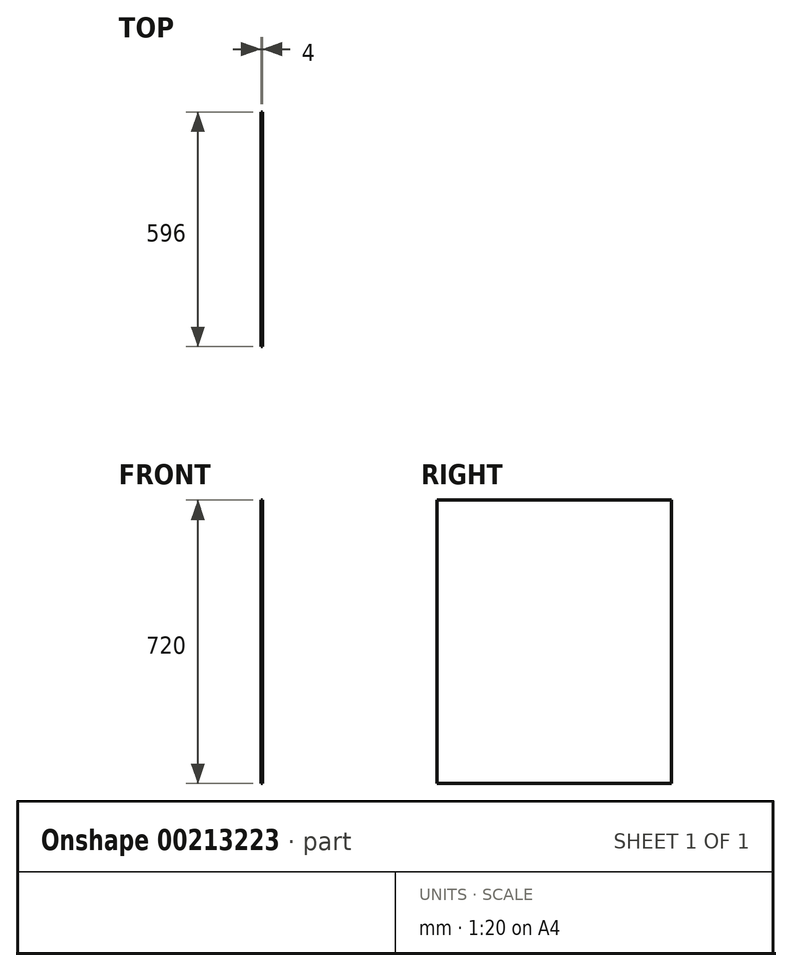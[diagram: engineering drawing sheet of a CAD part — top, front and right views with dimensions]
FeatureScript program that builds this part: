
annotation { "Feature Type Name" : "Feature", "Feature Type Description" : "" }
export const myFeature = defineFeature(function(context is Context, id is Id, definition is map)
    precondition{}
    {
        {
            var Q0;
            Q0=qCreatedBy(makeId("Right.planeOp"),FACE);
            var sketch = newSketch(context, id + "F0", { "sketchPlane" : qUnion([Q0])});
            skLineSegment(sketch, "E0.bottom", {"start": v(298, 360) * mm, "end": v(-298, 360) * mm});
            skLineSegment(sketch, "E0.top", {"start": v(298, -360) * mm, "end": v(-298, -360) * mm});
            skLineSegment(sketch, "E0.left", {"start": v(298, 360) * mm, "end": v(298, -360) * mm});
            skLineSegment(sketch, "E0.right", {"start": v(-298, 360) * mm, "end": v(-298, -360) * mm});
            skPoint(sketch, "E0.middle", {"position": v(0, 0) * mm});
            skSolve(sketch);
        }
        {
            var Q0;
            Q0=makeQuery(id+"F0.imprint","IMPRINT",FACE,{"disambiguationData":[TD([[makeQuery(id+"F0.imprint","IMPRINT",EDGE,{"derivedFrom":sQuery(id+"F0.wireOp",EDGE,"E0.bottom")}),1.0]])]});
            extrude(context, id + "F1", {"entities" : qUnion([Q0]), "endBound" : BoundingType.SYMMETRIC, "depth" : 4 * mm});
        }
    });
